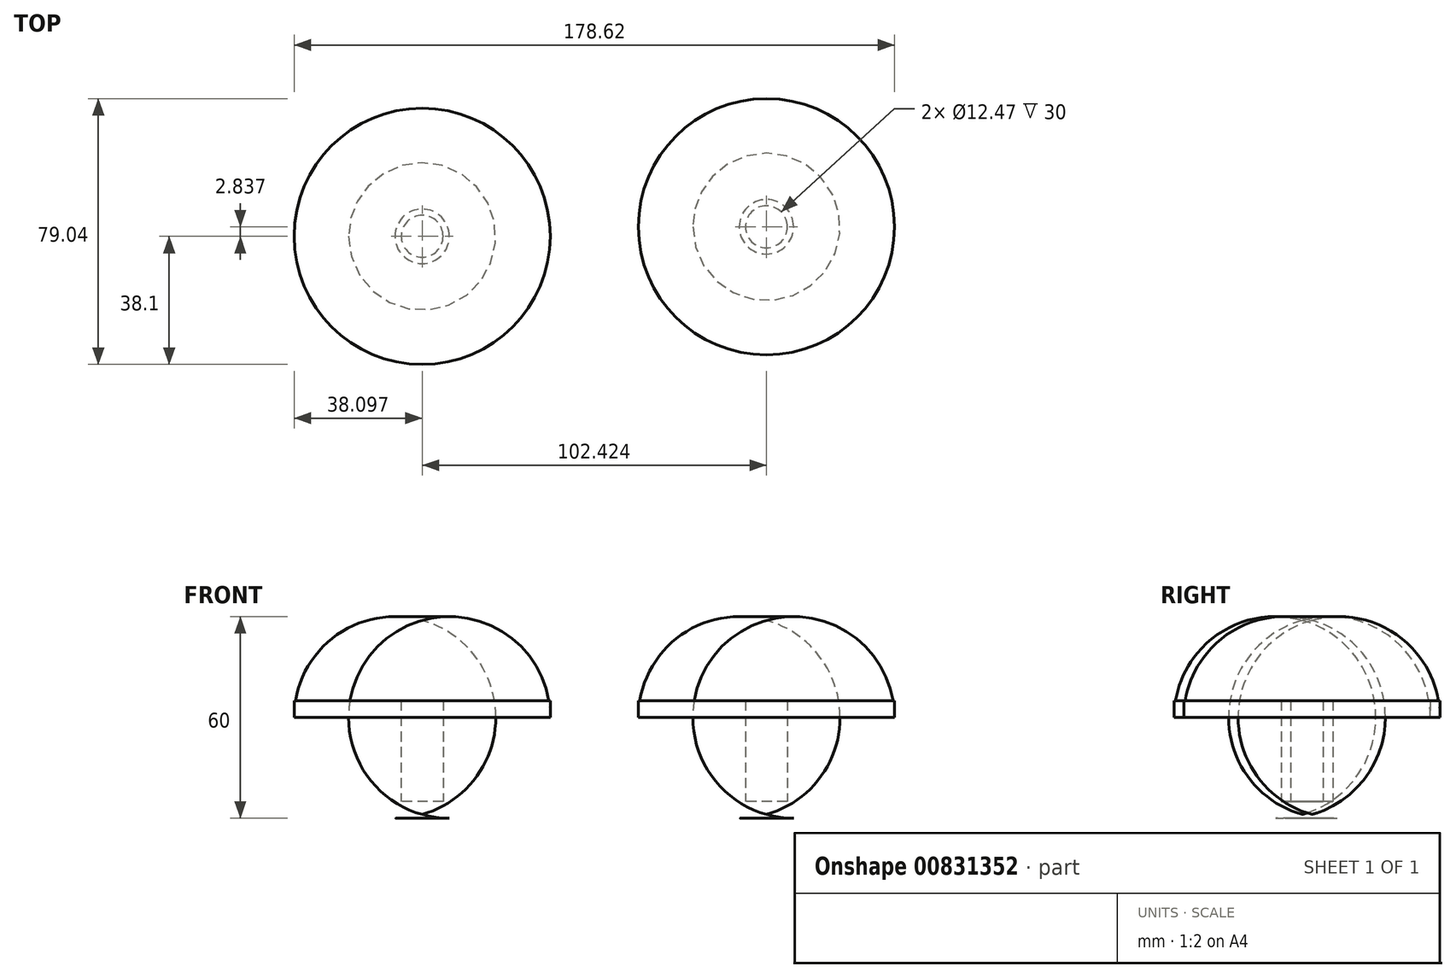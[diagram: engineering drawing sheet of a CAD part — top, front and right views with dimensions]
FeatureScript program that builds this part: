
annotation { "Feature Type Name" : "Feature", "Feature Type Description" : "" }
export const myFeature = defineFeature(function(context is Context, id is Id, definition is map)
    precondition{}
    {
        {
            var Q0;
            Q0=qCreatedBy(makeId("Top.planeOp"),FACE);
            var sketch = newSketch(context, id + "F0", { "sketchPlane" : qUnion([Q0])});
            skCircle(sketch, "E0", {"center": v(-52.06, 30.5) * mm, "radius": 38.1 * mm});
            skCircle(sketch, "E1", {"center": v(50.36, 33.34) * mm, "radius": 38.1 * mm});
            skCircle(sketch, "E2", {"center": v(-52.06, 30.5) * mm, "radius": 6.24 * mm});
            skCircle(sketch, "E3", {"center": v(50.36, 33.34) * mm, "radius": 6.24 * mm});
            skSolve(sketch);
        }
        {
            var Q0;
            Q0 = qSketchRegion(id + "F0", true);
            extrude(context, id + "F1", {"entities" : qUnion([Q0]), "depth" : 35 * mm, "offsetDistance" : 25.4 * mm});
        }
        {
            var Q0;
            Q0=makeQuery(id+"F1.opExtrude","CAP_EDGE",EDGE,{"disambiguationData":[OSD([sQuery(id+"F0.wireOp",EDGE,"E0")])],"isStart":true});
            var Q1;
            Q1=makeQuery(id+"F1.opExtrude","CAP_EDGE",EDGE,{"disambiguationData":[OSD([sQuery(id+"F0.wireOp",EDGE,"E1")])],"isStart":true});
            fillet(context, id + "F2", {"entities" : qUnion([Q0, Q1]), "radius" : 30 * mm, "tangentPropagation" : true, "allowEdgeOverflow" : false});
        }
        {
            var Q0;
            Q0=makeQuery(id+"F0.imprint","IMPRINT",FACE,{"disambiguationData":[TD([[makeQuery(id+"F0.imprint","IMPRINT",EDGE,{"derivedFrom":sQuery(id+"F0.wireOp",EDGE,"E2")}),1.0]])]});
            var Q1;
            Q1=makeQuery(id+"F0.imprint","IMPRINT",FACE,{"disambiguationData":[TD([[makeQuery(id+"F0.imprint","IMPRINT",EDGE,{"derivedFrom":sQuery(id+"F0.wireOp",EDGE,"E3")}),1.0]])]});
            extrude(context, id + "F3", {"entities" : qUnion([Q0, Q1]), "operationType" : NewBodyOperationType.ADD, "depth" : 5 * mm, "offsetDistance" : 25.4 * mm});
        }
    });
